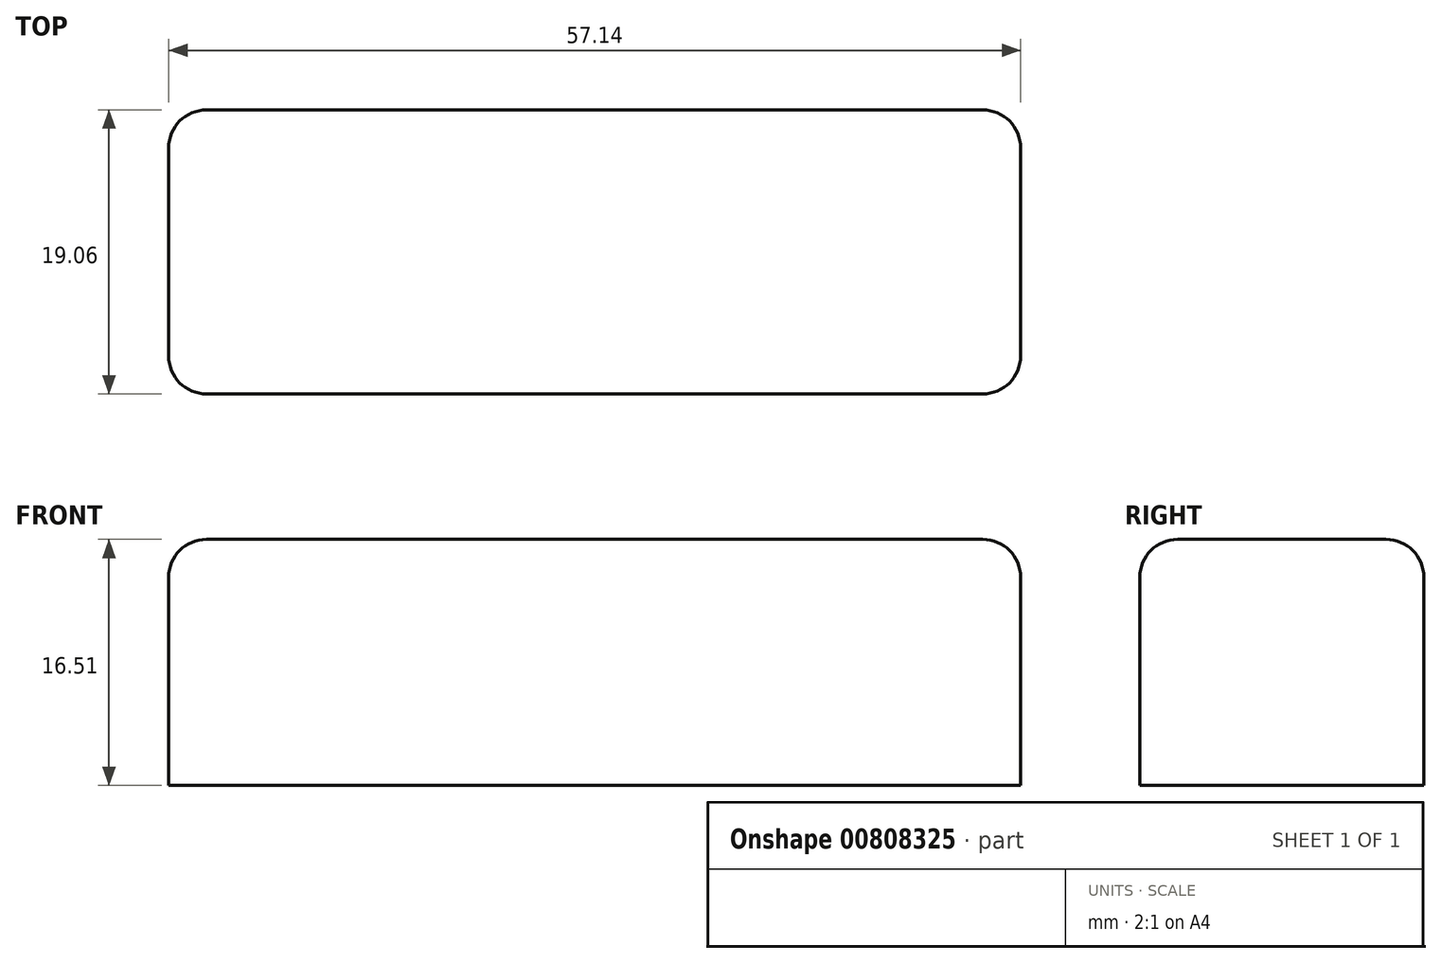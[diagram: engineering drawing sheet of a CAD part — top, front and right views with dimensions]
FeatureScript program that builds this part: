
annotation { "Feature Type Name" : "Feature", "Feature Type Description" : "" }
export const myFeature = defineFeature(function(context is Context, id is Id, definition is map)
    precondition{}
    {
        {
            var Q0;
            Q0=qCreatedBy(makeId("Top.planeOp"),FACE);
            var sketch = newSketch(context, id + "F0", { "sketchPlane" : qUnion([Q0])});
            skLineSegment(sketch, "E0.bottom", {"start": v(28.57, -9.52) * mm, "end": v(-28.58, -9.53) * mm});
            skLineSegment(sketch, "E0.top", {"start": v(28.57, 9.53) * mm, "end": v(-28.58, 9.52) * mm});
            skLineSegment(sketch, "E0.left", {"start": v(28.57, -9.52) * mm, "end": v(28.57, 9.53) * mm});
            skLineSegment(sketch, "E0.right", {"start": v(-28.58, -9.53) * mm, "end": v(-28.58, 9.52) * mm});
            skPoint(sketch, "E0.middle", {"position": v(0, 0) * mm});
            skSolve(sketch);
        }
        {
            var Q0;
            Q0 = qSketchRegion(id + "F0", true);
            extrude(context, id + "F1", {"entities" : qUnion([Q0]), "depth" : 16.5 * mm, "offsetDistance" : 25.4 * mm});
        }
        {
            var Q0;
            Q0=makeQuery(id+"F1.opExtrude","CAP_EDGE",EDGE,{"disambiguationData":[OSD([sQuery(id+"F0.wireOp",EDGE,"E0.bottom")])],"isStart":false});
            var Q1;
            Q1=makeQuery(id+"F1.opExtrude","CAP_EDGE",EDGE,{"disambiguationData":[OSD([sQuery(id+"F0.wireOp",EDGE,"E0.top")])],"isStart":false});
            var Q2;
            Q2=makeQuery(id+"F1.opExtrude","CAP_EDGE",EDGE,{"disambiguationData":[OSD([sQuery(id+"F0.wireOp",EDGE,"E0.left")])],"isStart":false});
            var Q3;
            Q3=makeQuery(id+"F1.opExtrude","SWEPT_EDGE",EDGE,{"disambiguationData":[OSD([sQuery(id+"F0.wireOp",EDGE,"E0.bottom"),sQuery(id+"F0.wireOp",EDGE,"E0.left")])]});
            var Q4;
            Q4=makeQuery(id+"F1.opExtrude","SWEPT_EDGE",EDGE,{"disambiguationData":[OSD([sQuery(id+"F0.wireOp",EDGE,"E0.top"),sQuery(id+"F0.wireOp",EDGE,"E0.left")])]});
            var Q5;
            Q5=makeQuery(id+"F1.opExtrude","SWEPT_EDGE",EDGE,{"disambiguationData":[OSD([sQuery(id+"F0.wireOp",EDGE,"E0.top"),sQuery(id+"F0.wireOp",EDGE,"E0.right")])]});
            var Q6;
            Q6=makeQuery(id+"F1.opExtrude","CAP_EDGE",EDGE,{"disambiguationData":[OSD([sQuery(id+"F0.wireOp",EDGE,"E0.right")])],"isStart":false});
            var Q7;
            Q7=makeQuery(id+"F1.opExtrude","SWEPT_EDGE",EDGE,{"disambiguationData":[OSD([sQuery(id+"F0.wireOp",EDGE,"E0.bottom"),sQuery(id+"F0.wireOp",EDGE,"E0.right")])]});
            fillet(context, id + "F2", {"entities" : qUnion([Q0, Q1, Q2, Q3, Q4, Q5, Q6, Q7]), "radius" : 2.54 * mm, "tangentPropagation" : true, "allowEdgeOverflow" : false});
        }
    });
